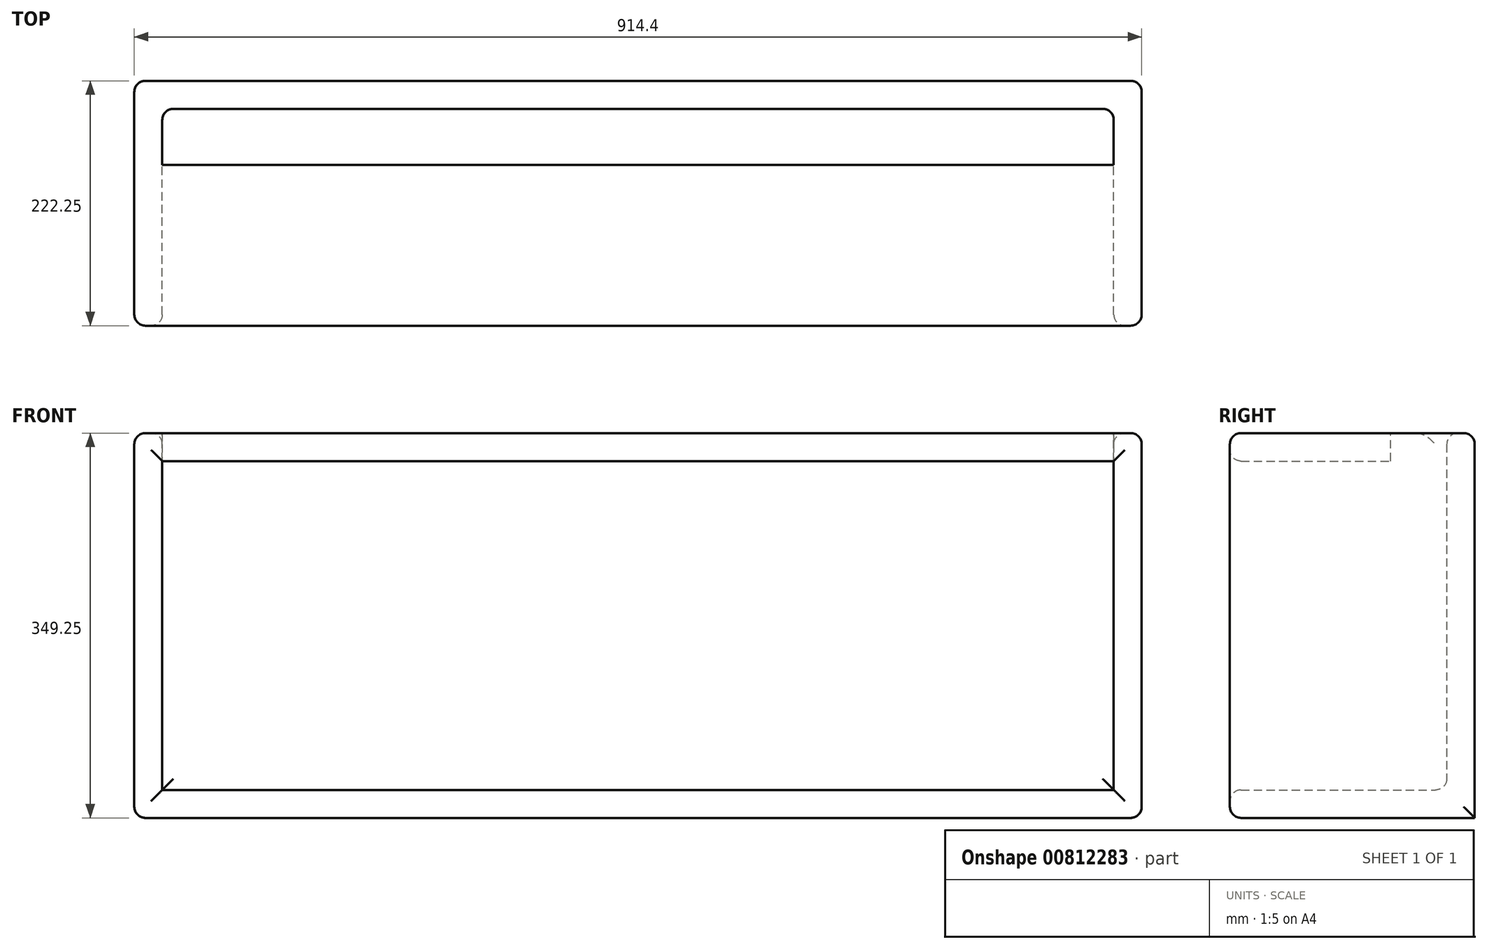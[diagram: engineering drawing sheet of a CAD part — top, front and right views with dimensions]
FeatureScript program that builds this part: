
annotation { "Feature Type Name" : "Feature", "Feature Type Description" : "" }
export const myFeature = defineFeature(function(context is Context, id is Id, definition is map)
    precondition{}
    {
        {
            var Q0;
            Q0=qCreatedBy(makeId("Front.planeOp"),FACE);
            var sketch = newSketch(context, id + "F0", { "sketchPlane" : qUnion([Q0])});
            skLineSegment(sketch, "E0.bottom", {"start": v(457.2, 174.63) * mm, "end": v(-457.2, 174.63) * mm});
            skLineSegment(sketch, "E0.top", {"start": v(457.2, -174.62) * mm, "end": v(-457.2, -174.62) * mm});
            skLineSegment(sketch, "E0.left", {"start": v(457.2, 174.63) * mm, "end": v(457.2, -174.63) * mm});
            skLineSegment(sketch, "E0.right", {"start": v(-457.2, 174.63) * mm, "end": v(-457.2, -174.62) * mm});
            skPoint(sketch, "E0.middle", {"position": v(0, 0) * mm});
            skSolve(sketch);
        }
        {
            var Q0;
            Q0=makeQuery(id+"F0.imprint","IMPRINT",FACE,{"disambiguationData":[TD([[makeQuery(id+"F0.imprint","IMPRINT",EDGE,{"derivedFrom":sQuery(id+"F0.wireOp",EDGE,"E0.bottom")}),1.0]])]});
            extrude(context, id + "F1", {"entities" : qUnion([Q0]), "depth" : 222.25 * mm, "offsetDistance" : 25.4 * mm});
        }
        {
            var Q0;
            Q0=makeQuery(id+"F1.opExtrude","CAP_FACE",FACE,{"disambiguationData":[OSD([sQuery(id+"F0.wireOp",EDGE,"E0.bottom"),sQuery(id+"F0.wireOp",EDGE,"E0.top"),sQuery(id+"F0.wireOp",EDGE,"E0.left"),sQuery(id+"F0.wireOp",EDGE,"E0.right")])],"isStart":false});
            shell(context, id + "F2", {"entities" : qUnion([Q0]), "thickness" : 25.4 * mm});
        }
        {
            var Q0;
            Q0=makeQuery(id+"F1.opExtrude","SWEPT_FACE",FACE,{"disambiguationData":[OSD([sQuery(id+"F0.wireOp",EDGE,"E0.bottom")])]});
            var sketch = newSketch(context, id + "F3", { "sketchPlane" : qUnion([Q0])});
            skLineSegment(sketch, "E1", {"start": v(-457.2, -25.4) * mm, "end": v(457.2, -25.4) * mm});
            skLineSegment(sketch, "E2", {"start": v(-457.2, -76.2) * mm, "end": v(457.2, -76.2) * mm});
            skLineSegment(sketch, "E3", {"start": v(457.2, -25.4) * mm, "end": v(457.2, -76.2) * mm});
            skLineSegment(sketch, "E4", {"start": v(-457.2, -25.4) * mm, "end": v(-457.2, -76.2) * mm});
            skLineSegment(sketch, "E5", {"start": v(431.8, -25.4) * mm, "end": v(431.8, -76.2) * mm});
            skLineSegment(sketch, "E6", {"start": v(-431.8, -25.4) * mm, "end": v(-431.8, -76.2) * mm});
            skSolve(sketch);
        }
        {
            var Q0;
            {var subQ0=sQuery(id+"F3.wireOp",EDGE,"E5");Q0=makeQuery(id+"F3.imprint","IMPRINT",FACE,{"disambiguationData":[TD([[makeQuery(id+"F3.imprint","IMPRINT",EDGE,{"derivedFrom":subQ0}),-1.0]])]});}
            extrude(context, id + "F4", {"entities" : qUnion([Q0]), "operationType" : NewBodyOperationType.REMOVE, "oppositeDirection" : true, "depth" : 25.4 * mm, "offsetDistance" : 25.4 * mm});
        }
        {
            var Q0;
            Q0=makeQuery(id+"F1.opExtrude","SWEPT_EDGE",EDGE,{"disambiguationData":[OSD([sQuery(id+"F0.wireOp",EDGE,"E0.bottom"),sQuery(id+"F0.wireOp",EDGE,"E0.left")])]});
            var Q1;
            Q1=makeQuery(id+"F1.opExtrude","CAP_EDGE",EDGE,{"disambiguationData":[OSD([sQuery(id+"F0.wireOp",EDGE,"E0.bottom")])],"isStart":true});
            var Q2;
            Q2=makeQuery(id+"F1.opExtrude","CAP_EDGE",EDGE,{"disambiguationData":[OSD([sQuery(id+"F0.wireOp",EDGE,"E0.left")])],"isStart":true});
            var Q3;
            Q3=makeQuery(id+"F1.opExtrude","SWEPT_FACE",FACE,{"disambiguationData":[OSD([sQuery(id+"F0.wireOp",EDGE,"E0.left")])]});
            var Q4;
            Q4=makeQuery(id+"F1.opExtrude","SWEPT_EDGE",EDGE,{"disambiguationData":[OSD([sQuery(id+"F0.wireOp",EDGE,"E0.top"),sQuery(id+"F0.wireOp",EDGE,"E0.left")])]});
            var Q5;
            Q5=makeQuery(id+"F4.boolean.opBoolean","MERGE",FACE,{"derivedFrom":[makeQuery(id+"F2.opShell","OFFSET_FACE",FACE,{"disambiguationData":[OSD([sQuery(id+"F0.wireOp",EDGE,"E0.bottom"),sQuery(id+"F0.wireOp",EDGE,"E0.top"),sQuery(id+"F0.wireOp",EDGE,"E0.left"),sQuery(id+"F0.wireOp",EDGE,"E0.right")])]}),makeQuery(id+"F4.opExtrude","SWEPT_FACE",FACE,{"disambiguationData":[OSD([sQuery(id+"F3.wireOp",EDGE,"E1")])]})]});
            var Q6;
            Q6=makeQuery(id+"F1.opExtrude","CAP_EDGE",EDGE,{"disambiguationData":[OSD([sQuery(id+"F0.wireOp",EDGE,"E0.bottom")])],"isStart":false});
            var Q7;
            Q7=makeQuery(id+"F1.opExtrude","CAP_FACE",FACE,{"disambiguationData":[OSD([sQuery(id+"F0.wireOp",EDGE,"E0.bottom"),sQuery(id+"F0.wireOp",EDGE,"E0.top"),sQuery(id+"F0.wireOp",EDGE,"E0.left"),sQuery(id+"F0.wireOp",EDGE,"E0.right")])],"isStart":false});
            var Q8;
            Q8=makeQuery(id+"F1.opExtrude","CAP_EDGE",EDGE,{"disambiguationData":[OSD([sQuery(id+"F0.wireOp",EDGE,"E0.right")])],"isStart":true});
            var Q9;
            Q9=makeQuery(id+"F1.opExtrude","SWEPT_EDGE",EDGE,{"disambiguationData":[OSD([sQuery(id+"F0.wireOp",EDGE,"E0.bottom"),sQuery(id+"F0.wireOp",EDGE,"E0.right")])]});
            var Q10;
            Q10=makeQuery(id+"F1.opExtrude","SWEPT_EDGE",EDGE,{"disambiguationData":[OSD([sQuery(id+"F0.wireOp",EDGE,"E0.top"),sQuery(id+"F0.wireOp",EDGE,"E0.right")])]});
            var Q11;
            Q11=makeQuery(id+"F1.opExtrude","CAP_EDGE",EDGE,{"disambiguationData":[OSD([sQuery(id+"F0.wireOp",EDGE,"E0.right")])],"isStart":false});
            var Q12;
            Q12=makeQuery(id+"F4.boolean.opBoolean","COPY",EDGE,{"derivedFrom":makeQuery(id+"F4.opExtrude","CAP_EDGE",EDGE,{"disambiguationData":[OSD([sQuery(id+"F3.wireOp",EDGE,"E2")])],"isStart":true})});
            fillet(context, id + "F5", {"entities" : qUnion([Q0, Q1, Q2, Q3, Q4, Q5, Q6, Q7, Q8, Q9, Q10, Q11, Q12]), "radius" : 10.16 * mm, "tangentPropagation" : true, "allowEdgeOverflow" : false});
        }
    });
